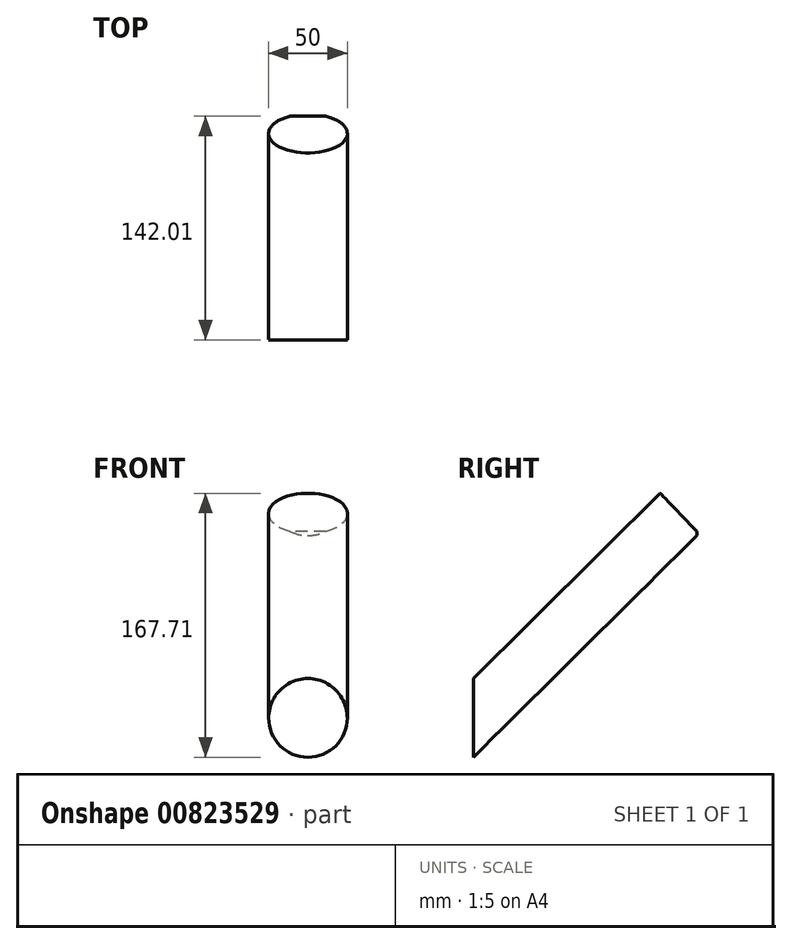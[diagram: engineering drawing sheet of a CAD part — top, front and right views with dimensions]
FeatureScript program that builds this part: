
annotation { "Feature Type Name" : "Feature", "Feature Type Description" : "" }
export const myFeature = defineFeature(function(context is Context, id is Id, definition is map)
    precondition{}
    {
        {
            var Q0;
            Q0=qCreatedBy(makeId("Right.planeOp"),FACE);
            var sketch = newSketch(context, id + "F0", { "sketchPlane" : qUnion([Q0])});
            skLineSegment(sketch, "E0", {"start": v(0, 0) * mm, "end": v(142, 140.83) * mm});
            skSolve(sketch);
        }
        {
            var Q0;
            Q0=qCreatedBy(makeId("Front.planeOp"),FACE);
            var sketch = newSketch(context, id + "F1", { "sketchPlane" : qUnion([Q0])});
            skCircle(sketch, "E1", {"center": v(0, 0) * mm, "radius": 25 * mm});
            skSolve(sketch);
        }
        {
            var Q0;
            Q0=makeQuery(id+"F1.imprint","IMPRINT",FACE,{"disambiguationData":[TD([[makeQuery(id+"F1.imprint","IMPRINT",EDGE,{"derivedFrom":sQuery(id+"F1.wireOp",EDGE,"E1")}),1.0]])]});
            var Q1;
            Q1=sQuery(id+"F0.wireOp",EDGE,"E0");
            sweep(context, id + "F2", {"profiles" : qUnion([Q0]), "path" : qUnion([Q1])});
        }
        {
            var Q0;
            Q0=qCreatedBy(makeId("Right.planeOp"),FACE);
            var sketch = newSketch(context, id + "F3", { "sketchPlane" : qUnion([Q0])});
            skLineSegment(sketch, "E2", {"start": v(143.18, 117.29) * mm, "end": v(114.13, 147.46) * mm});
            skLineSegment(sketch, "E3", {"start": v(114.13, 147.46) * mm, "end": v(148.34, 180.4) * mm});
            skLineSegment(sketch, "E4", {"start": v(148.34, 180.4) * mm, "end": v(143.18, 117.29) * mm});
            skSolve(sketch);
        }
        {
            var Q0;
            Q0 = qSketchRegion(id + "F3", true);
            extrude(context, id + "F4", {"entities" : qUnion([Q0]), "operationType" : NewBodyOperationType.REMOVE, "oppositeDirection" : true, "depth" : 49 * mm, "offsetDistance" : 25 * mm});
        }
        {
            var Q0;
            Q0 = qSketchRegion(id + "F3", true);
            extrude(context, id + "F5", {"entities" : qUnion([Q0]), "operationType" : NewBodyOperationType.REMOVE, "depth" : 92 * mm, "offsetDistance" : 25 * mm});
        }
    });
